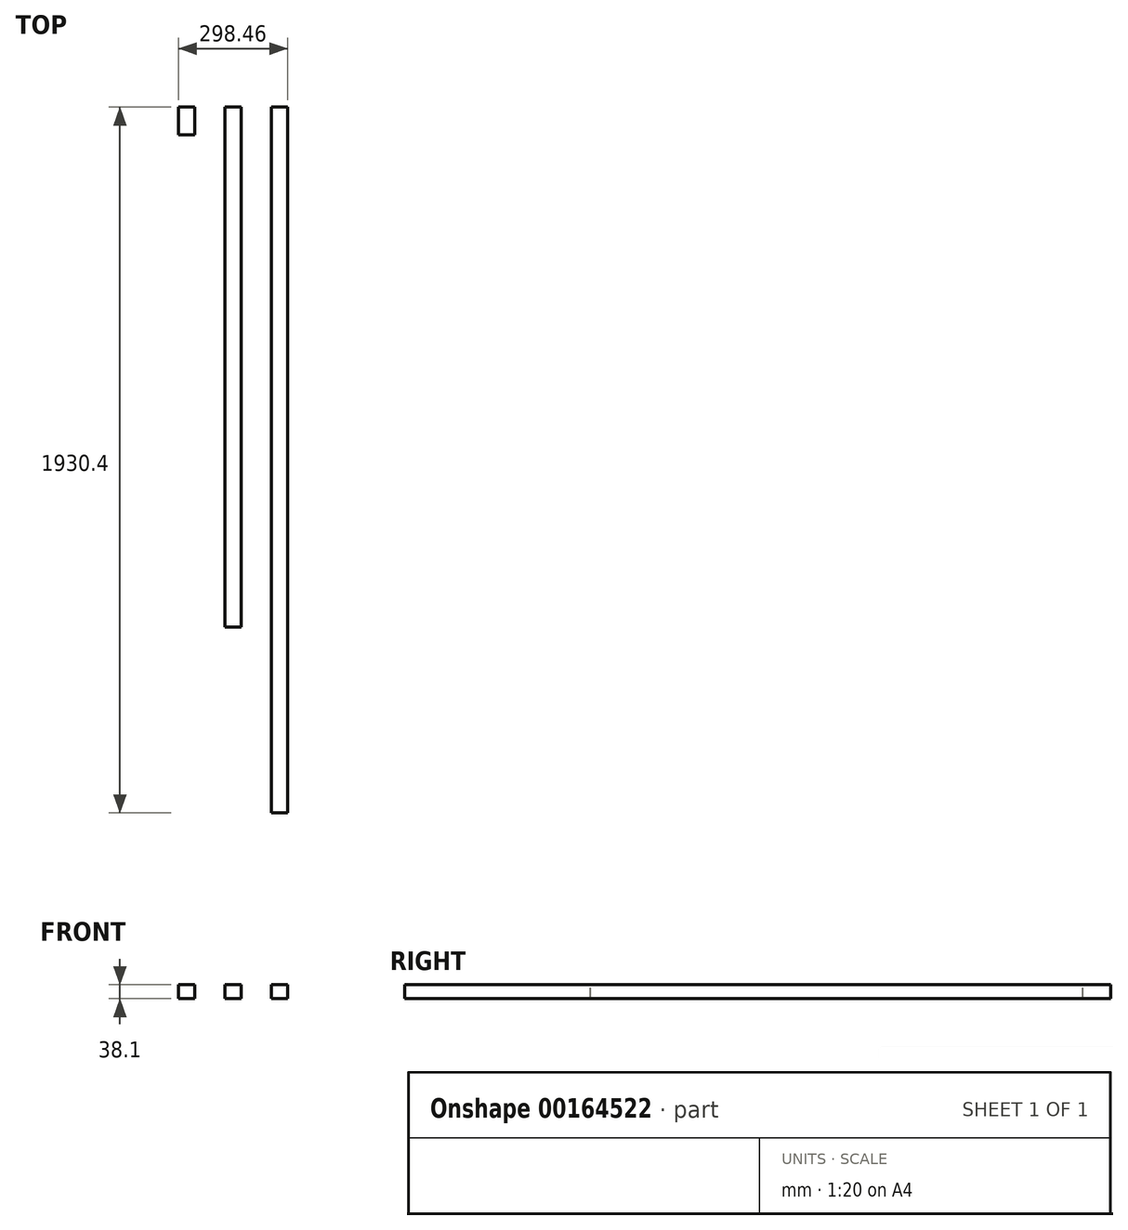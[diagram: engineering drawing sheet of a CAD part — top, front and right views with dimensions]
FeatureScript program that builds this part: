
annotation { "Feature Type Name" : "Feature", "Feature Type Description" : "" }
export const myFeature = defineFeature(function(context is Context, id is Id, definition is map)
    precondition{}
    {
        {
            var Q0;
            Q0=qCreatedBy(makeId("Front.planeOp"),FACE);
            var sketch = newSketch(context, id + "F0", { "sketchPlane" : qUnion([Q0])});
            skLineSegment(sketch, "E0.bottom", {"start": v(22.23, -19.05) * mm, "end": v(-22.23, -19.05) * mm});
            skLineSegment(sketch, "E0.top", {"start": v(22.23, 19.05) * mm, "end": v(-22.23, 19.05) * mm});
            skLineSegment(sketch, "E0.left", {"start": v(22.23, -19.05) * mm, "end": v(22.23, 19.05) * mm});
            skLineSegment(sketch, "E0.right", {"start": v(-22.23, -19.05) * mm, "end": v(-22.23, 19.05) * mm});
            skPoint(sketch, "E0.middle", {"position": v(0, 0) * mm});
            skSolve(sketch);
        }
        {
            var Q0;
            Q0 = qSketchRegion(id + "F0", true);
            extrude(context, id + "F1", {"entities" : qUnion([Q0]), "depth" : 76.2 * mm});
        }
        {
            var Q0;
            Q0=makeQuery(id+"F1.opExtrude","SWEPT_BODY",BODY,{"disambiguationData":[OSD([sQuery(id+"F0.wireOp",EDGE,"E0.bottom"),sQuery(id+"F0.wireOp",EDGE,"E0.top"),sQuery(id+"F0.wireOp",EDGE,"E0.left"),sQuery(id+"F0.wireOp",EDGE,"E0.right")])]});
            transform(context, id + "F2", {"entities" : qUnion([Q0]), "transformType" : TransformType.TRANSLATION_3D, "dx" : 127 * mm, "dy" : 0 * mm, "dz" : 0 * mm, "makeCopy" : true});
        }
        {
            var Q0;
            Q0=makeQuery(id+"F2.opPattern","COPY",FACE,{"derivedFrom":makeQuery(id+"F1.opExtrude","CAP_FACE",FACE,{"disambiguationData":[OSD([sQuery(id+"F0.wireOp",EDGE,"E0.bottom"),sQuery(id+"F0.wireOp",EDGE,"E0.top"),sQuery(id+"F0.wireOp",EDGE,"E0.left"),sQuery(id+"F0.wireOp",EDGE,"E0.right")])],"isStart":false}),"instanceName":"1"});
            extrude(context, id + "F3", {"entities" : qUnion([Q0]), "operationType" : NewBodyOperationType.ADD, "depth" : 1346.2 * mm});
        }
        {
            var Q0;
            Q0=makeQuery(id+"F1.opExtrude","SWEPT_BODY",BODY,{"disambiguationData":[OSD([sQuery(id+"F0.wireOp",EDGE,"E0.bottom"),sQuery(id+"F0.wireOp",EDGE,"E0.top"),sQuery(id+"F0.wireOp",EDGE,"E0.left"),sQuery(id+"F0.wireOp",EDGE,"E0.right")])]});
            transform(context, id + "F4", {"entities" : qUnion([Q0]), "transformType" : TransformType.TRANSLATION_3D, "dx" : 254 * mm, "dy" : 0 * mm, "dz" : 0 * mm, "makeCopy" : true});
        }
        {
            var Q0;
            Q0=makeQuery(id+"F4.opPattern","COPY",FACE,{"derivedFrom":makeQuery(id+"F1.opExtrude","CAP_FACE",FACE,{"disambiguationData":[OSD([sQuery(id+"F0.wireOp",EDGE,"E0.bottom"),sQuery(id+"F0.wireOp",EDGE,"E0.top"),sQuery(id+"F0.wireOp",EDGE,"E0.left"),sQuery(id+"F0.wireOp",EDGE,"E0.right")])],"isStart":false}),"instanceName":"1"});
            extrude(context, id + "F5", {"entities" : qUnion([Q0]), "operationType" : NewBodyOperationType.ADD, "depth" : 1854.2 * mm});
        }
    });
